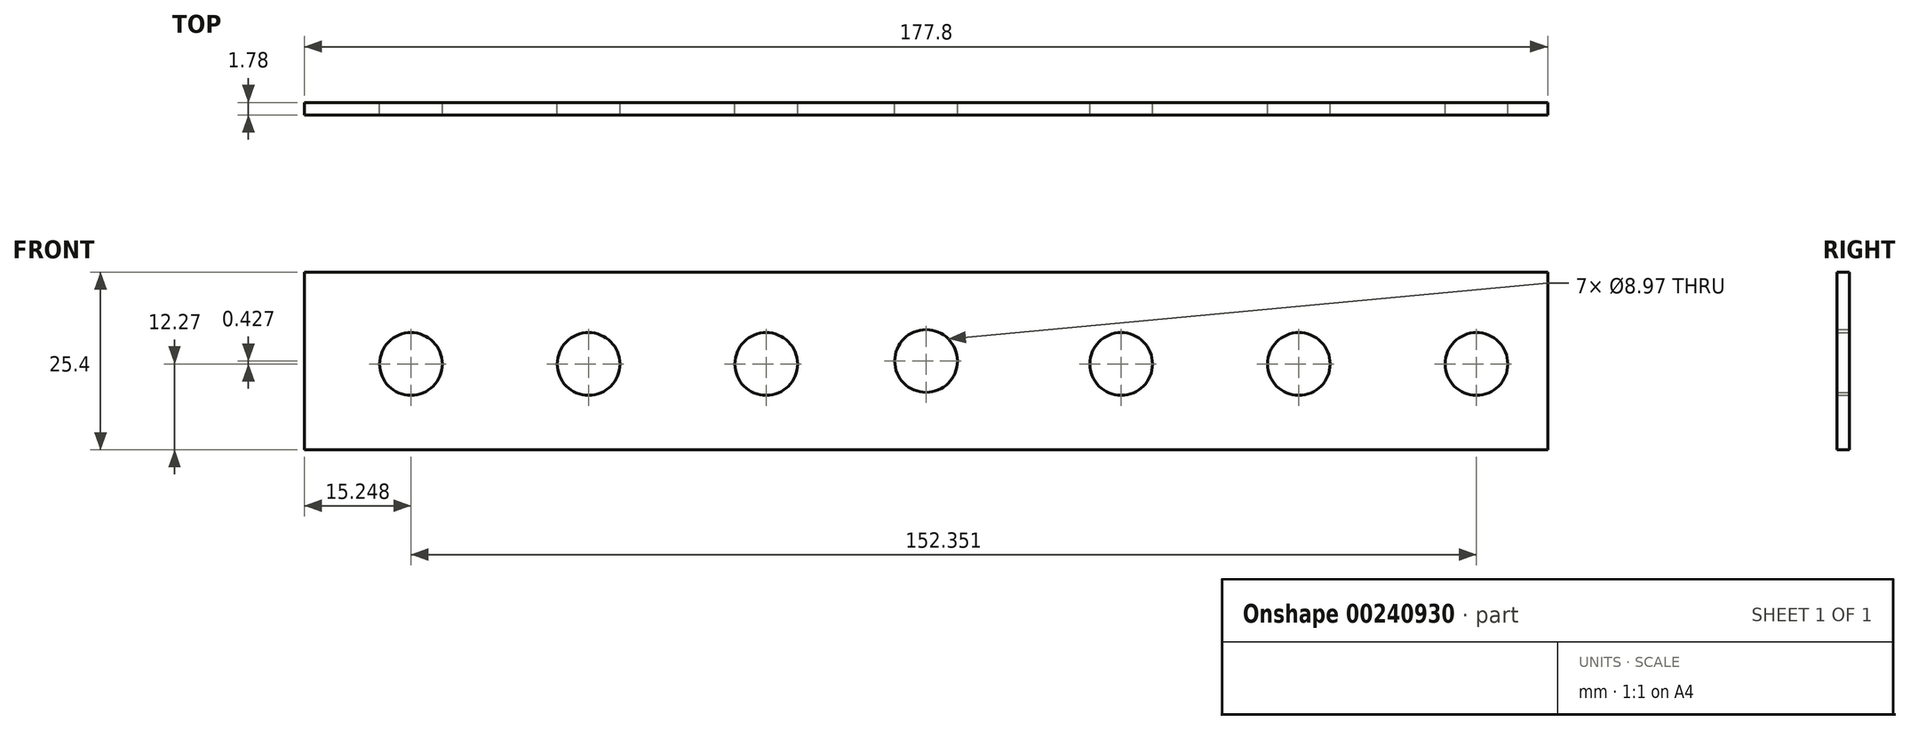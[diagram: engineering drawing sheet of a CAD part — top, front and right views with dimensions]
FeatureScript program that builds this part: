
annotation { "Feature Type Name" : "Feature", "Feature Type Description" : "" }
export const myFeature = defineFeature(function(context is Context, id is Id, definition is map)
    precondition{}
    {
        {
            var Q0;
            Q0=qCreatedBy(makeId("Front.planeOp"),FACE);
            var sketch = newSketch(context, id + "F0", { "sketchPlane" : qUnion([Q0])});
            skLineSegment(sketch, "E0.bottom", {"start": v(88.9, -28.12) * mm, "end": v(-88.9, -28.12) * mm});
            skLineSegment(sketch, "E0.top", {"start": v(88.9, -2.72) * mm, "end": v(-88.9, -2.72) * mm});
            skLineSegment(sketch, "E0.left", {"start": v(88.9, -28.12) * mm, "end": v(88.9, -2.72) * mm});
            skLineSegment(sketch, "E0.right", {"start": v(-88.9, -28.12) * mm, "end": v(-88.9, -2.72) * mm});
            skPoint(sketch, "E0.middle", {"position": v(0, -15.42) * mm});
            skCircle(sketch, "E1", {"center": v(-73.65, -15.85) * mm, "radius": 4.49 * mm});
            skCircle(sketch, "E2", {"center": v(-48.25, -15.85) * mm, "radius": 4.49 * mm});
            skCircle(sketch, "E3", {"center": v(-22.85, -15.85) * mm, "radius": 4.49 * mm});
            skCircle(sketch, "E4", {"center": v(0, -15.42) * mm, "radius": 4.49 * mm});
            skCircle(sketch, "E5", {"center": v(27.9, -15.85) * mm, "radius": 4.49 * mm});
            skCircle(sketch, "E6", {"center": v(53.3, -15.85) * mm, "radius": 4.49 * mm});
            skCircle(sketch, "E7", {"center": v(78.7, -15.85) * mm, "radius": 4.49 * mm});
            skPoint(sketch, "E8.start.orphan", {"position": v(-43.76, -15.85) * mm});
            skSolve(sketch);
        }
        {
            var Q0;
            Q0 = qSketchRegion(id + "F0", true);
            extrude(context, id + "F1", {"entities" : qUnion([Q0]), "depth" : 1.78 * mm});
        }
    });
